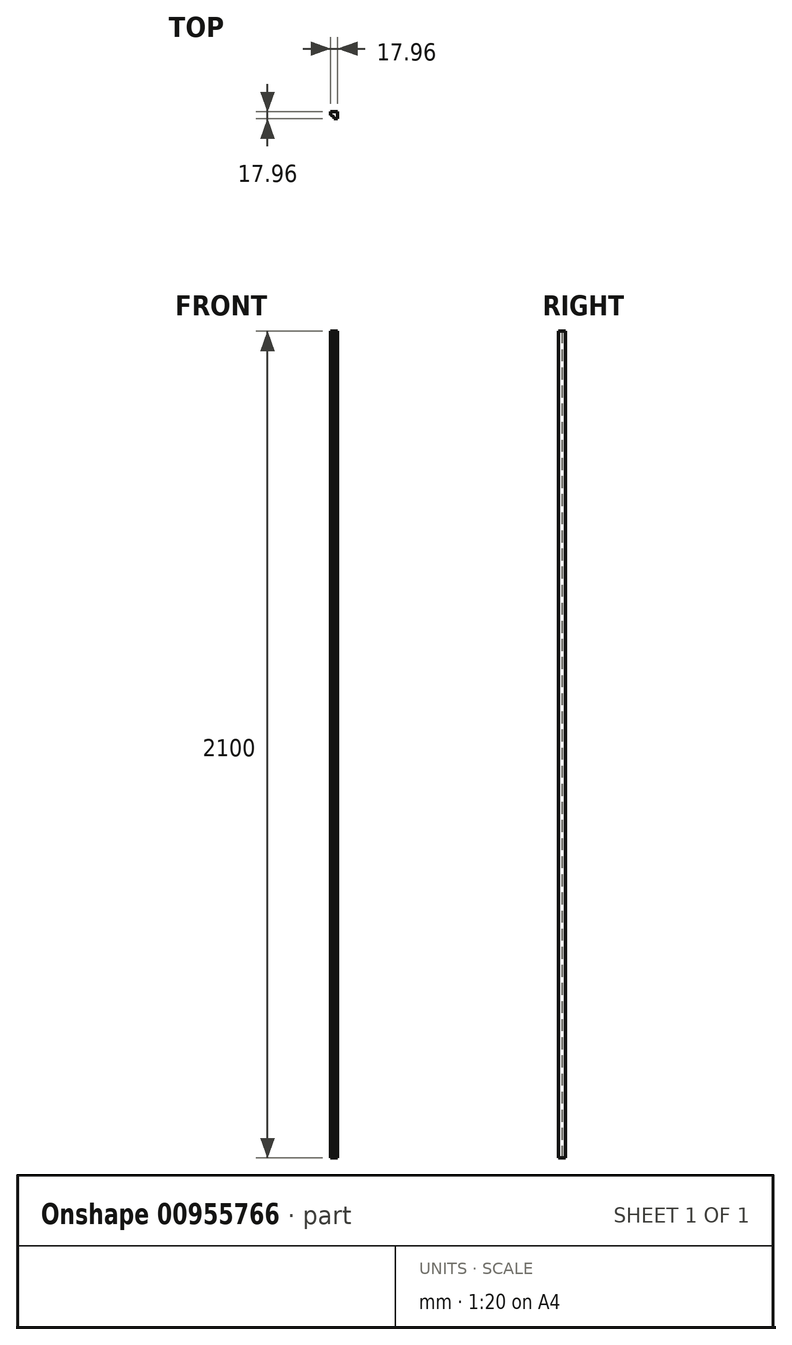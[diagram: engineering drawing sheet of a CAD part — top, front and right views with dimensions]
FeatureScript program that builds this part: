
annotation { "Feature Type Name" : "Feature", "Feature Type Description" : "" }
export const myFeature = defineFeature(function(context is Context, id is Id, definition is map)
    precondition{}
    {
        {
            var Q0;
            Q0=qCreatedBy(makeId("Top.planeOp"),FACE);
            var sketch = newSketch(context, id + "F0", { "sketchPlane" : qUnion([Q0])});
            skLineSegment(sketch, "E0.bottom", {"start": v(-39.54, 13.09) * mm, "end": v(-57.5, 13.09) * mm});
            skLineSegment(sketch, "E0.top", {"start": v(-39.54, 31.05) * mm, "end": v(-57.5, 31.05) * mm});
            skLineSegment(sketch, "E0.left", {"start": v(-39.54, 13.09) * mm, "end": v(-39.54, 31.05) * mm});
            skLineSegment(sketch, "E0.right", {"start": v(-57.5, 13.09) * mm, "end": v(-57.5, 31.05) * mm});
            skPoint(sketch, "E0.middle", {"position": v(-48.52, 22.07) * mm});
            skLineSegment(sketch, "E1", {"start": v(-48.52, 22.07) * mm, "end": v(-57.5, 22.07) * mm});
            skCircle(sketch, "E2", {"center": v(-57.5, 13.09) * mm, "radius": 8.98 * mm});
            skSolve(sketch);
        }
        {
            var Q0;
            {var subQ1=sQuery(id+"F0.wireOp",EDGE,"E0.top");Q0=makeQuery(id+"F0.imprint","IMPRINT",FACE,{"disambiguationData":[TD([[makeQuery(id+"F0.imprint","IMPRINT",EDGE,{"derivedFrom":subQ1}),1.0]])]});}
            extrude(context, id + "F1", {"entities" : qUnion([Q0]), "depth" : 2100 * mm, "offsetDistance" : 25.4 * mm});
        }
    });
